# Revit family: Urinal-Flush_Actuator_Sensor-KOHLER-Patio-K-20368T
name_source: partatom
category: Plumbing Fixtures
units: mm (PartAtom-declared; Revit-internal decimal feet)

## family parameters
Cut with Voids When Loaded = No
Host = Face
OmniClass Number = 23.31.25.00
OmniClass Title = Toilet and Bath Specialties
Part Type = Normal
Room Calculation Point = No
Round Connector Dimension = Use Diameter
Shared = No

## types (2) — shared parameters
ADA Compliant = No
Apparent Load = 0 VA
Assembly Code = D2010
CW Connection = Yes
Cold Water Inlet = Cold Water Inlet
Cold Water Outlet = Cold Water Outlet
Date Modified = 10/03/2023
Default Elevation = 36"
Drain Included = No
Electrical Connector = Yes
Electrical Note = One Dedicated Circuit Required
Finish = Kohler-Plastic-CP-Polished_Chrome
Flow Rate = 0 GPM
HW Connection = No
Height = 5"
Hot Water Inlet = Hot Water Inlet
Length = 3 13/16"
Manufacturer = Kohler Co.
Master Format 2014 = 22 41 39
Master Format 2014 Name = Residential Faucets, Supplies, and Trim
Material = Plastic
Pressure = 80.00 psi
Product Name = Patio
URL = http://www.kohler.com.cn
Vent Connection = No
Voltage = 220 V
Waste Connection = No
Waste Water Outlet = Waste Water Outlet
WaterSense Certified = No
Width = 5"

## per-type parameters (varying)
| type | Description | Model | Type |
| 2W, CP-Polished Chrome | Urinal Sensor 0.5/1.0 LPF | K-23368T-2W-CP | 2 |
| 2, CP-Polished Chrome | Urinal Sensor 2.5 LPF | K-23368T-2-CP | 1 |

## geometry (parser evidence)
native form markers: Sweep x6
no freeform markers — native parametric forms only
